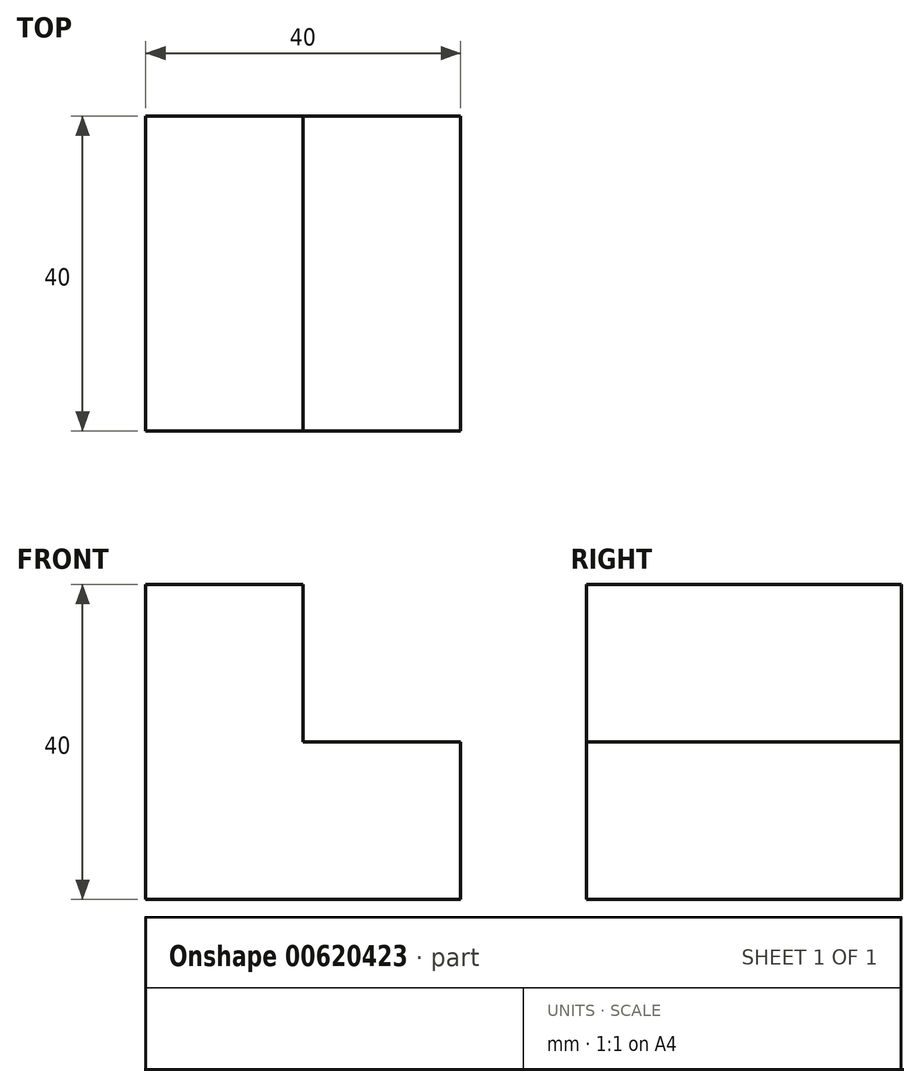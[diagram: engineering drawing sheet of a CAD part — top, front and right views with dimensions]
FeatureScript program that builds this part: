
annotation { "Feature Type Name" : "Feature", "Feature Type Description" : "" }
export const myFeature = defineFeature(function(context is Context, id is Id, definition is map)
    precondition{}
    {
        {
            var Q0;
            Q0=qCreatedBy(makeId("Front.planeOp"),FACE);
            var sketch = newSketch(context, id + "F0", { "sketchPlane" : qUnion([Q0])});
            skLineSegment(sketch, "E0", {"start": v(-60.27, 30.1) * mm, "end": v(-60.27, -9.9) * mm});
            skLineSegment(sketch, "E1", {"start": v(-60.27, -9.9) * mm, "end": v(-20.27, -9.9) * mm});
            skLineSegment(sketch, "E2", {"start": v(-20.27, -9.9) * mm, "end": v(-20.27, 10.1) * mm});
            skLineSegment(sketch, "E3", {"start": v(-20.27, 10.1) * mm, "end": v(-40.27, 10.1) * mm});
            skLineSegment(sketch, "E4", {"start": v(-40.27, 10.1) * mm, "end": v(-40.27, 30.1) * mm});
            skLineSegment(sketch, "E5", {"start": v(-40.27, 30.1) * mm, "end": v(-60.27, 30.1) * mm});
            skSolve(sketch);
        }
        {
            var Q0;
            Q0 = qSketchRegion(id + "F0", true);
            extrude(context, id + "F1", {"entities" : qUnion([Q0]), "depth" : 40 * mm, "offsetDistance" : 25 * mm});
        }
    });
